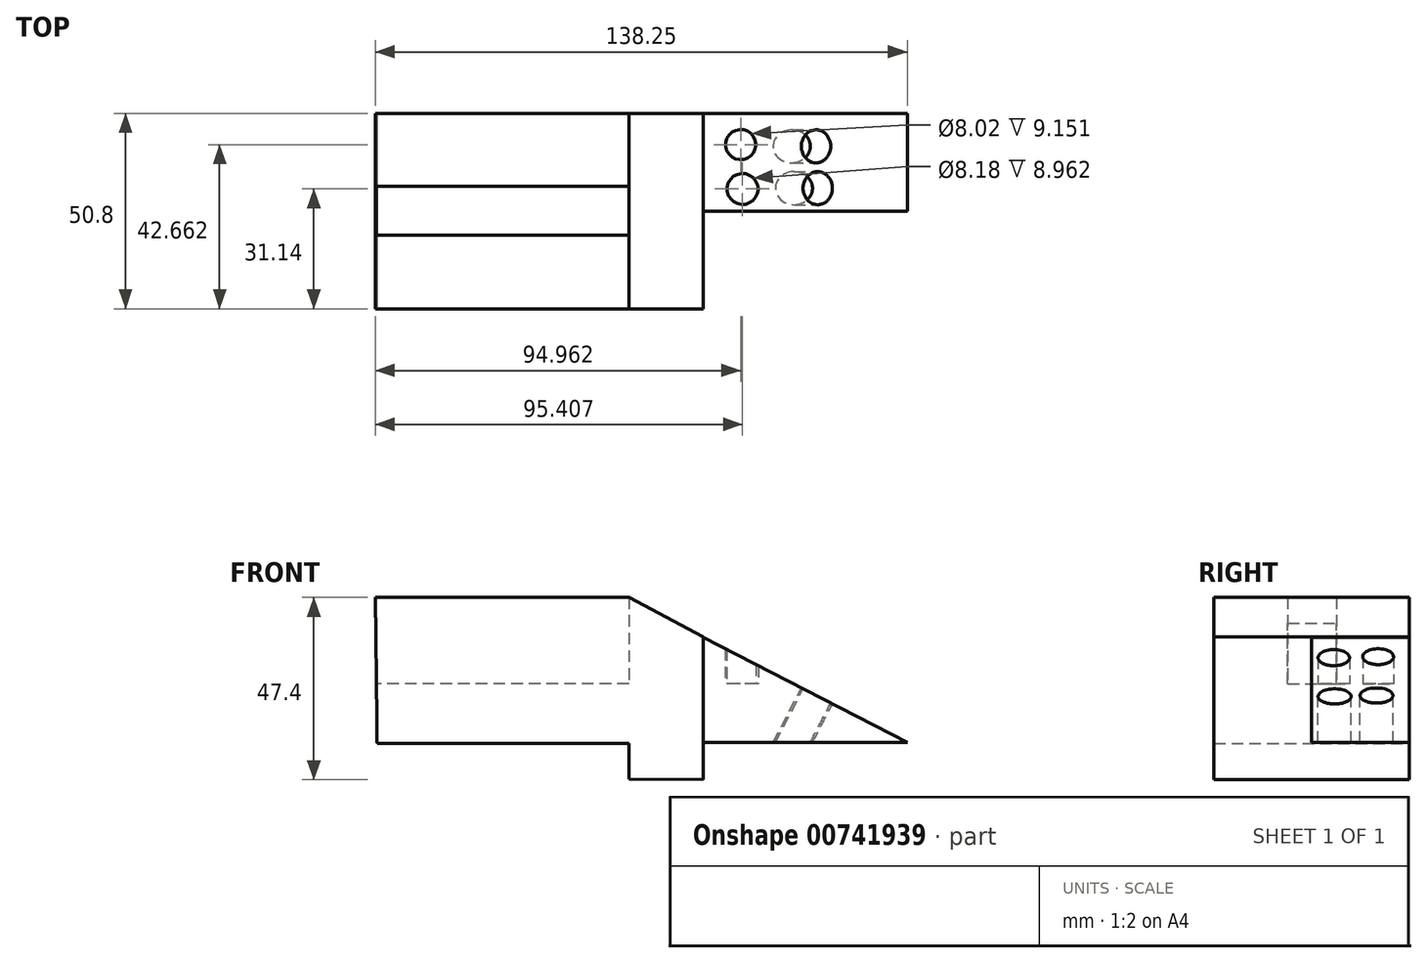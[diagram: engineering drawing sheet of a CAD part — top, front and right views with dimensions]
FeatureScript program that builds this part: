
annotation { "Feature Type Name" : "Feature", "Feature Type Description" : "" }
export const myFeature = defineFeature(function(context is Context, id is Id, definition is map)
    precondition{}
    {
        {
            var Q0;
            Q0=qCreatedBy(makeId("Front.planeOp"),FACE);
            var sketch = newSketch(context, id + "F0", { "sketchPlane" : qUnion([Q0])});
            skLineSegment(sketch, "E0", {"start": v(-65.49, 22.02) * mm, "end": v(0, 22.02) * mm});
            skLineSegment(sketch, "E1", {"start": v(0, 22.02) * mm, "end": v(0, -15.27) * mm});
            skLineSegment(sketch, "E2", {"start": v(0, -15.27) * mm, "end": v(-65.49, -15.27) * mm});
            skLineSegment(sketch, "E3", {"start": v(-65.49, -15.27) * mm, "end": v(-65.49, 22.02) * mm});
            skLineSegment(sketch, "E4", {"start": v(0, 22.02) * mm, "end": v(19.3, 12.09) * mm});
            skLineSegment(sketch, "E5", {"start": v(19.3, 12.09) * mm, "end": v(19.3, -24.72) * mm});
            skLineSegment(sketch, "E6", {"start": v(19.3, -24.72) * mm, "end": v(0, -24.72) * mm});
            skLineSegment(sketch, "E7", {"start": v(0, -24.72) * mm, "end": v(0, -15.27) * mm});
            skLineSegment(sketch, "E8", {"start": v(19.3, -15.27) * mm, "end": v(64.42, -15.27) * mm});
            skLineSegment(sketch, "E9", {"start": v(64.42, -15.27) * mm, "end": v(72.36, -15.27) * mm});
            skLineSegment(sketch, "E10", {"start": v(72.36, -15.27) * mm, "end": v(19.3, 12.09) * mm});
            skSolve(sketch);
        }
        {
            var Q0;
            Q0=makeQuery(id+"F0.imprint","IMPRINT",FACE,{"disambiguationData":[TD([[makeQuery(id+"F0.imprint","IMPRINT",EDGE,{"derivedFrom":sQuery(id+"F0.wireOp",EDGE,"E0")}),-1.0]])]});
            var Q1;
            Q1=makeQuery(id+"F0.imprint","IMPRINT",FACE,{"disambiguationData":[TD([[makeQuery(id+"F0.imprint","IMPRINT",EDGE,{"derivedFrom":sQuery(id+"F0.wireOp",EDGE,"E1")}),1.0]])]});
            extrude(context, id + "F1", {"entities" : qUnion([Q0, Q1]), "depth" : 50.8 * mm, "offsetDistance" : 25.4 * mm});
        }
        {
            var Q0;
            {var subQ2=sQuery(id+"F0.wireOp",EDGE,"E8");Q0=makeQuery(id+"F0.imprint","IMPRINT",FACE,{"disambiguationData":[TD([[makeQuery(id+"F0.imprint","IMPRINT",EDGE,{"derivedFrom":subQ2}),1.0]])]});}
            extrude(context, id + "F2", {"entities" : qUnion([Q0]), "operationType" : NewBodyOperationType.ADD, "depth" : 25.4 * mm, "offsetDistance" : 25.4 * mm});
        }
        {
            var Q0;
            Q0=qCreatedBy(makeId("Front.planeOp"),FACE);
            var sketch = newSketch(context, id + "F3", { "sketchPlane" : qUnion([Q0])});
            skLineSegment(sketch, "E11", {"start": v(-65.9, 22.47) * mm, "end": v(0, 22.47) * mm});
            skLineSegment(sketch, "E12", {"start": v(0, 22.47) * mm, "end": v(0, -15.51) * mm});
            skLineSegment(sketch, "E13", {"start": v(0, -15.51) * mm, "end": v(-65.4, -15.51) * mm});
            skLineSegment(sketch, "E14", {"start": v(-65.4, -15.51) * mm, "end": v(-65.9, 22.47) * mm});
            skLineSegment(sketch, "E15", {"start": v(0, -24.77) * mm, "end": v(0, 22.47) * mm});
            skLineSegment(sketch, "E16", {"start": v(0, 22.47) * mm, "end": v(19.33, 12.24) * mm});
            skLineSegment(sketch, "E17", {"start": v(19.33, 12.24) * mm, "end": v(19.33, -24.93) * mm});
            skLineSegment(sketch, "E18", {"start": v(19.33, -24.93) * mm, "end": v(0, -24.77) * mm});
            skLineSegment(sketch, "E19", {"start": v(19.33, 12.24) * mm, "end": v(72.73, -15.68) * mm});
            skLineSegment(sketch, "E20", {"start": v(72.73, -15.68) * mm, "end": v(19.33, -15.68) * mm});
            skSolve(sketch);
        }
        {
            var Q0;
            Q0=makeQuery(id+"F3.imprint","IMPRINT",FACE,{"disambiguationData":[TD([[makeQuery(id+"F3.imprint","IMPRINT",EDGE,{"derivedFrom":sQuery(id+"F3.wireOp",EDGE,"E11")}),-1.0]])]});
            var Q1;
            Q1=makeQuery(id+"F3.imprint","IMPRINT",FACE,{"disambiguationData":[TD([[makeQuery(id+"F3.imprint","IMPRINT",EDGE,{"derivedFrom":sQuery(id+"F3.wireOp",EDGE,"E12")}),1.0]])]});
            extrude(context, id + "F4", {"entities" : qUnion([Q0, Q1]), "operationType" : NewBodyOperationType.ADD, "depth" : 50.8 * mm, "offsetDistance" : 25.4 * mm});
        }
        {
            var Q0;
            {var subQ2=sQuery(id+"F0.wireOp",EDGE,"E8");Q0=makeQuery(id+"F0.imprint","IMPRINT",FACE,{"disambiguationData":[TD([[makeQuery(id+"F0.imprint","IMPRINT",EDGE,{"derivedFrom":subQ2}),1.0]])]});}
            extrude(context, id + "F5", {"entities" : qUnion([Q0]), "operationType" : NewBodyOperationType.ADD, "depth" : 25.4 * mm, "offsetDistance" : 25.4 * mm});
        }
        {
            var Q0;
            Q0=qCreatedBy(makeId("Top.planeOp"),FACE);
            var sketch = newSketch(context, id + "F6", { "sketchPlane" : qUnion([Q0])});
            skLineSegment(sketch, "E21.bottom", {"start": v(0, -31.65) * mm, "end": v(-65.8, -31.65) * mm});
            skLineSegment(sketch, "E21.top", {"start": v(0, -19) * mm, "end": v(-65.8, -19) * mm});
            skLineSegment(sketch, "E21.left", {"start": v(0, -31.65) * mm, "end": v(0, -19) * mm});
            skLineSegment(sketch, "E21.right", {"start": v(-65.8, -31.65) * mm, "end": v(-65.8, -19) * mm});
            skSolve(sketch);
        }
        {
            var Q0;
            Q0 = qSketchRegion(id + "F6", true);
            extrude(context, id + "F7", {"entities" : qUnion([Q0]), "operationType" : NewBodyOperationType.REMOVE, "depth" : 38.1 * mm, "offsetDistance" : 25.4 * mm});
        }
        {
            var Q0;
            Q0=qCreatedBy(makeId("Top.planeOp"),FACE);
            var sketch = newSketch(context, id + "F8", { "sketchPlane" : qUnion([Q0])});
            skCircle(sketch, "E22", {"center": v(29.52, -19.66) * mm, "radius": 4.09 * mm});
            skCircle(sketch, "E23", {"center": v(29.07, -8.14) * mm, "radius": 4 * mm});
            skCircle(sketch, "E24", {"center": v(55.28, -19.76) * mm, "radius": 3.02 * mm});
            skCircle(sketch, "E25", {"center": v(54.86, -8.44) * mm, "radius": 3.2 * mm});
            skSolve(sketch);
        }
        {
            var Q0;
            Q0 = qSketchRegion(id + "F8", true);
            extrude(context, id + "F9", {"entities" : qUnion([Q0]), "operationType" : NewBodyOperationType.REMOVE, "depth" : 50.8 * mm, "offsetDistance" : 25.4 * mm});
        }
        {
            var Q0;
            Q0=makeQuery(id+"F2.opExtrude","SWEPT_FACE",FACE,{"disambiguationData":[OSD([sQuery(id+"F0.wireOp",EDGE,"E10")])]});
            var sketch = newSketch(context, id + "F10", { "sketchPlane" : qUnion([Q0])});
            skCircle(sketch, "E26", {"center": v(45.11, -19.46) * mm, "radius": 4.3 * mm});
            skCircle(sketch, "E27", {"center": v(44.6, -8.56) * mm, "radius": 4.29 * mm});
            skSolve(sketch);
        }
        {
            var Q0;
            Q0 = qSketchRegion(id + "F10", true);
            extrude(context, id + "F11", {"entities" : qUnion([Q0]), "operationType" : NewBodyOperationType.REMOVE, "oppositeDirection" : true, "depth" : 25.4 * mm, "offsetDistance" : 25.4 * mm});
        }
    });
